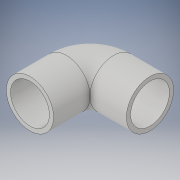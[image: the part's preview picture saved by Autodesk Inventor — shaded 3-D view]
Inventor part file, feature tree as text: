
AUTODESK INVENTOR PART (.ipt)
format: ipt  version: 2018 (Build 220112000, 112)  size: 183,296 bytes
history: native  units: in
note: dims shown in document units (in); Inventor stores cm internally (conversion verified against a paired STEP export)
features: sketch x6, extrude x4, plane x3, revolve x2, other x1
ambient origin geometry x8: Origin, YZ Plane, XZ Plane, XY Plane, X Axis, Y Axis, Z Axis, Center Point
bodies: Solid1 (feature_tree)
feature tree (16):
  extrude  "Extrusion1"  Depth=1.237in TaperAngle=0.0deg
  sketch  "Sketch2"  dims[d3=-0.6184in d4=0.8025in]
  plane  "Work Plane1"
  extrude  "Extrusion2"  Depth=0.8025in
  sketch  "Sketch4"  dims[d8=1.321in d9=0.0in]
  sketch  "Sketch5"  dims[d10=0.0in d11=90.0deg]
  plane  "Work Plane2"
  plane  "Work Plane3"
  revolve  "Revolution1"  [1 undecoded]
  extrude  "Extrusion3"  TaperAngle=0.0deg  [1 undecoded]
  other  "Work Axis1"
  revolve  "Revolution2"  Angle=90.0deg
  extrude  "Extrusion4"  Depth=1.252in
  sketch  "Sketch1"  dims[d0=1.605in d1=1.237in d2=0.0in]
  sketch  "Sketch3"  dims[d5=1.237in d6=0.0in d7=1.321in]
  sketch  "Sketch6"  dims[d12=1.252in d13=0.0in d14=1.0in d15=90.0deg d16=1.252in d17=0.0in]
note: 2 required parameter values undecoded (feature->parameter linkage not recoverable at this tier; creation-order binding heuristic only, values carry confidence <= 0.55)